# Revit family: 756-106-691-DN700-800
name_source: partatom
category: Pipe Accessories
units: mm (PartAtom-declared; Revit-internal decimal feet)

## family parameters
Always vertical = Yes
Cut with Voids When Loaded = No
Part Type = Valve - Breaks Into
Round Connector Dimension = Use Diameter
Shared = No
Work Plane-Based = No

## types (4) — shared parameters
Body_wallthickness = 10 mm  [stored 0.0328084 ft]
C_rod = 39 mm  [stored 0.127953 ft]
DN0700_PN10 = 756-0700-1-04106
DN0700_PN16 = 756-0700-1-14106
DN0800_PN10 = 756-0800-1-04106
DN0800_PN16 = 756-0800-1-14106
DN700 = Yes
DN800 = Yes
Description_ = AVK_DOUBLE_ECCENTRIC_BUTTERFLY_VALVE,LONG
Disc_width = 40 mm  [stored 0.131234 ft]
Disk_1 = 40 mm  [stored 0.131234 ft]
Disk_2 = 40 mm  [stored 0.131234 ft]
Flange_Thickness = 40 mm  [stored 0.131234 ft]
HW_rod_Dia = 30 mm  [stored 0.0984252 ft]
Offset = 3 mm  [stored 0.00984252 ft]
Pin_dia = 60 mm  [stored 0.19685 ft]
RF_Cut_Thickness = 5 mm  [stored 0.0164042 ft]
Rib_depth = 15 mm  [stored 0.0492126 ft]
Search_table = 756-106-691-DN700-800
URL_product_pages = https://www.avkvalves.com

## per-type parameters (varying)
- DN0700_PN10: Bottom_Depth=1050 mm; Bottom_width=395 mm; D=285 mm  [stored 0.935039 ft]; DN=700 mm; Disc_Dia=690 mm; Flange_OD=448 mm; Gear_box_Mount_Flange_thickness=30 mm  [stored 0.0984252 ft]; Gear_box_Mount_Flange_width=102 mm; Gear_box_Mount_width=62 mm  [stored 0.203412 ft]; Gear_box_width=133 mm  [stored 0.436352 ft]; H1=532 mm; H2=550 mm; HW_Connecting_Rib=570 mm; HW_Connecting_Rib_ref=587 mm; HW_Ref=110 mm  [stored 0.360892 ft]; HW_height=381 mm; Hand_wheel_rod=33 mm  [stored 0.108268 ft]; ID (Radius)=350 mm; L=430 mm; L1=127 mm; L2=133 mm  [stored 0.436352 ft]; Pin_Depth=798 mm; Pin_width=215 mm; Rf_Dia=397 mm; Rib_height=407 mm; Rib_height_2=85 mm; Rib_width=350 mm; Rib_width_2=204 mm  [stored 0.669291 ft]; W1=448 mm; W2=641 mm; W3=533 mm; W4=543 mm; W5=396 mm
- DN0700_PN16: Bottom_Depth=1050 mm; Bottom_width=427 mm; D=335 mm; DN=700 mm; Disc_Dia=690 mm; Flange_OD=455 mm; Gear_box_Mount_Flange_thickness=30 mm  [stored 0.0984252 ft]; Gear_box_Mount_Flange_width=107 mm  [stored 0.35105 ft]; Gear_box_Mount_width=66 mm  [stored 0.216535 ft]; Gear_box_width=139 mm; H1=532 mm; H2=550 mm; HW_Connecting_Rib=670 mm; HW_Connecting_Rib_ref=587 mm; HW_Ref=110 mm  [stored 0.360892 ft]; HW_height=502 mm; Hand_wheel_rod=35 mm; ID (Radius)=350 mm; L=430 mm; L1=127 mm; L2=133 mm  [stored 0.436352 ft]; Pin_Depth=805 mm; Pin_width=215 mm; Rf_Dia=397 mm; Rib_height=414 mm; Rib_height_2=77 mm  [stored 0.252625 ft]; Rib_width=350 mm; Rib_width_2=214 mm  [stored 0.7021 ft]; W1=455 mm; W2=641 mm; W3=533 mm; W4=543 mm; W5=517 mm
- DN0800_PN10: Bottom_Depth=1200 mm; Bottom_width=460 mm; D=285 mm  [stored 0.935039 ft]; DN=800 mm; Disc_Dia=788 mm; Flange_OD=508 mm; Gear_box_Mount_Flange_thickness=40 mm  [stored 0.131234 ft]; Gear_box_Mount_Flange_width=112 mm; Gear_box_Mount_width=68 mm  [stored 0.223097 ft]; Gear_box_width=145 mm; H1=603 mm; H2=620 mm; HW_Connecting_Rib=570 mm; HW_Connecting_Rib_ref=657 mm; HW_Ref=125 mm  [stored 0.410105 ft]; HW_height=381 mm; Hand_wheel_rod=36 mm  [stored 0.11811 ft]; ID (Radius)=400 mm; L=470 mm; L1=156 mm  [stored 0.511811 ft]; L2=162 mm  [stored 0.531496 ft]; Pin_Depth=908 mm; Pin_width=235 mm  [stored 0.770997 ft]; Rf_Dia=450 mm; Rib_height=461 mm; Rib_height_2=96 mm; Rib_width=390 mm; Rib_width_2=223 mm  [stored 0.731627 ft]; W1=508 mm; W2=711 mm; W3=627 mm; W4=636 mm; W5=396 mm
- DN0800_PN16: Bottom_Depth=1200 mm; Bottom_width=492 mm; D=385 mm; DN=800 mm; Disc_Dia=788 mm; Flange_OD=513 mm; Gear_box_Mount_Flange_thickness=40 mm  [stored 0.131234 ft]; Gear_box_Mount_Flange_width=116 mm  [stored 0.380577 ft]; Gear_box_Mount_width=72 mm  [stored 0.23622 ft]; Gear_box_width=151 mm; H1=603 mm; H2=620 mm; HW_Connecting_Rib=770 mm; HW_Connecting_Rib_ref=657 mm; HW_Ref=125 mm  [stored 0.410105 ft]; HW_height=502 mm; Hand_wheel_rod=38 mm; ID (Radius)=400 mm; L=470 mm; L1=156 mm  [stored 0.511811 ft]; L2=162 mm  [stored 0.531496 ft]; Pin_Depth=913 mm; Pin_width=235 mm  [stored 0.770997 ft]; Rf_Dia=450 mm; Rib_height=466 mm; Rib_height_2=91 mm; Rib_width=390 mm; Rib_width_2=232 mm  [stored 0.761155 ft]; W1=513 mm; W2=711 mm; W3=627 mm; W4=636 mm; W5=517 mm

note: [stored X ft] marks values corroborated as IEEE doubles in the binary element streams (Revit-internal decimal feet)

## geometry (parser evidence)
native form markers: Sweep x4
no freeform markers — native parametric forms only
